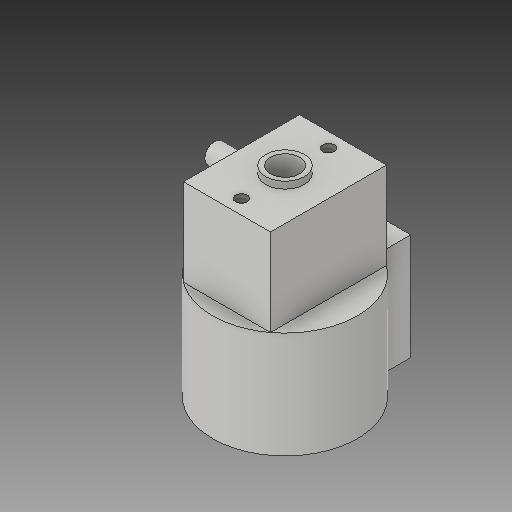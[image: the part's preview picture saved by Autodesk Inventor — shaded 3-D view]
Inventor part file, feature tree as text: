
AUTODESK INVENTOR PART (.ipt)
format: ipt  version: 2019 (Build 230136000, 136)  size: 175,104 bytes
history: native  units: in
note: dims shown in document units (in); Inventor stores cm internally (conversion verified against a paired STEP export)
features: sketch x6, extrude x5, hole x1
ambient origin geometry x8: Origin, YZ Plane, XZ Plane, XY Plane, X Axis, Y Axis, Z Axis, Center Point
bodies: Solid2 (feature_tree)
feature tree (12):
  extrude  "Extrusion3"  Depth=0.1181in
  extrude  "Extrusion4"  Depth=0.3937in
  extrude  "Extrusion5"  Depth=0.7874in TaperAngle=0.0deg
  hole  "Hole1"  [1 undecoded]
  extrude  "Extrusion6"  Depth=1.1811in
  extrude  "Extrusion7"  Depth=0.0276in
  sketch  "Sketch1"  dims[d0=0.5906in d1=0.1181in]
  sketch  "Sketch3"  dims[d2=0.3937in d4=0.3937in]
  sketch  "Sketch4"  dims[d15=0.1181in d16=0.7874in d17=0.0in]
  sketch  "Sketch5"  dims[d18=0.3543in d19=0.4724in]
  sketch  "Sketch6"  dims[d20=1.1811in d21=1.1811in]
  sketch  "Sketch7"  dims[d22=0.5906in d23=0.5906in d24=0.3543in d25=0.0in d26=0.0787in d27=0.0984in d28=0.0984in d29=0.0984in d30=0.0787in d31=0.0512in d32=0.3543in d33=0.0in d34=0.3543in d35=0.1772in d36=0.0481in d37=0.126in d38=0.1575in d39=0.0787in d40=90.0deg d41=0.2087in d42=0.8108in d43=0.2362in d44=0.0394in d45=0.0in d46=0.1575in d47=0.0276in d48=0.0in]
note: 1 required parameter value undecoded (feature->parameter linkage not recoverable at this tier; creation-order binding heuristic only, values carry confidence <= 0.55)
